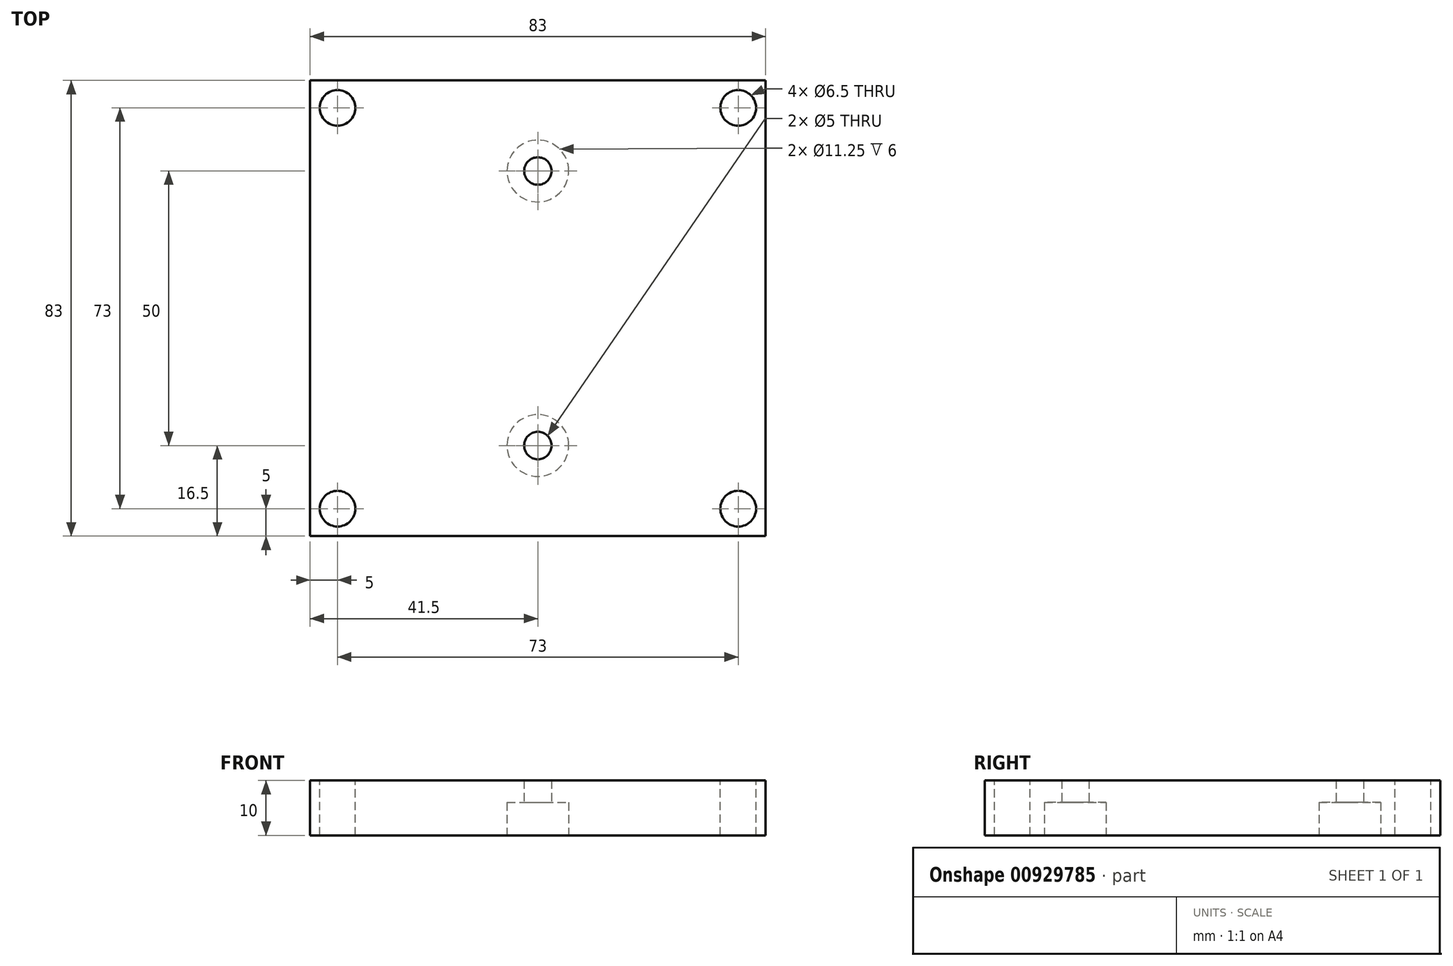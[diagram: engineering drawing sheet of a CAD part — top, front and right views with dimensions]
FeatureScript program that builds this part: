
annotation { "Feature Type Name" : "Feature", "Feature Type Description" : "" }
export const myFeature = defineFeature(function(context is Context, id is Id, definition is map)
    precondition{}
    {
        {
            var Q0;
            Q0=qCreatedBy(makeId("Top.planeOp"),FACE);
            var sketch = newSketch(context, id + "F0", { "sketchPlane" : qUnion([Q0])});
            skLineSegment(sketch, "E0.bottom", {"start": v(41.5, 41.5) * mm, "end": v(-41.5, 41.5) * mm});
            skLineSegment(sketch, "E0.top", {"start": v(41.5, -41.5) * mm, "end": v(-41.5, -41.5) * mm});
            skLineSegment(sketch, "E0.left", {"start": v(41.5, 41.5) * mm, "end": v(41.5, -41.5) * mm});
            skLineSegment(sketch, "E0.right", {"start": v(-41.5, 41.5) * mm, "end": v(-41.5, -41.5) * mm});
            skPoint(sketch, "E0.middle", {"position": v(0, 0) * mm});
            skSolve(sketch);
        }
        {
            var Q0;
            Q0 = qSketchRegion(id + "F0", true);
            extrude(context, id + "F1", {"entities" : qUnion([Q0]), "depth" : 10 * mm, "offsetDistance" : 25 * mm});
        }
        {
            var Q0;
            Q0=makeQuery(id+"F1.opExtrude","CAP_FACE",FACE,{"disambiguationData":[OSD([sQuery(id+"F0.wireOp",EDGE,"E0.bottom"),sQuery(id+"F0.wireOp",EDGE,"E0.top"),sQuery(id+"F0.wireOp",EDGE,"E0.left"),sQuery(id+"F0.wireOp",EDGE,"E0.right")])],"isStart":false});
            var sketch = newSketch(context, id + "F2", { "sketchPlane" : qUnion([Q0])});
            skLineSegment(sketch, "E1", {"start": v(71.1, 36.5) * mm, "end": v(-79.54, 36.5) * mm, "construction": true});
            skLineSegment(sketch, "E2", {"start": v(-78.9, -36.5) * mm, "end": v(83.67, -36.5) * mm, "construction": true});
            skLineSegment(sketch, "E3", {"start": v(-36.5, 85.44) * mm, "end": v(-36.5, -99.54) * mm, "construction": true});
            skLineSegment(sketch, "E4", {"start": v(36.5, 83.72) * mm, "end": v(36.5, -82.62) * mm, "construction": true});
            skCircle(sketch, "E5", {"center": v(-36.5, 36.5) * mm, "radius": 3.25 * mm});
            skCircle(sketch, "E6", {"center": v(-36.5, -36.5) * mm, "radius": 3.25 * mm});
            skCircle(sketch, "E7", {"center": v(36.5, -36.5) * mm, "radius": 3.25 * mm});
            skCircle(sketch, "E8", {"center": v(36.5, 36.5) * mm, "radius": 3.25 * mm});
            skSolve(sketch);
        }
        {
            var Q0;
            Q0 = qSketchRegion(id + "F2", true);
            extrude(context, id + "F3", {"entities" : qUnion([Q0]), "operationType" : NewBodyOperationType.REMOVE, "endBound" : BoundingType.UP_TO_NEXT, "oppositeDirection" : true, "depth" : 25 * mm, "offsetDistance" : 25 * mm});
        }
        {
            var Q0;
            Q0=makeQuery(id+"F1.opExtrude","CAP_FACE",FACE,{"disambiguationData":[OSD([sQuery(id+"F0.wireOp",EDGE,"E0.bottom"),sQuery(id+"F0.wireOp",EDGE,"E0.top"),sQuery(id+"F0.wireOp",EDGE,"E0.left"),sQuery(id+"F0.wireOp",EDGE,"E0.right")])],"isStart":true});
            var sketch = newSketch(context, id + "F4", { "sketchPlane" : qUnion([Q0])});
            skLineSegment(sketch, "E9", {"start": v(0, 41.5) * mm, "end": v(0, -41.5) * mm, "construction": true});
            skLineSegment(sketch, "E10", {"start": v(-41.5, 0) * mm, "end": v(41.5, 0) * mm, "construction": true});
            skLineSegment(sketch, "E11.0", {"start": v(-50, -25) * mm, "end": v(50, -25) * mm, "construction": true});
            skLineSegment(sketch, "E12.0", {"start": v(-50, 25) * mm, "end": v(50, 25) * mm, "construction": true});
            skLineSegment(sketch, "E13.0", {"start": v(46.5, 46.5) * mm, "end": v(-46.5, 46.5) * mm});
            skLineSegment(sketch, "E13.1", {"start": v(46.5, -46.5) * mm, "end": v(46.5, 46.5) * mm});
            skLineSegment(sketch, "E13.2", {"start": v(-46.5, -46.5) * mm, "end": v(46.5, -46.5) * mm});
            skLineSegment(sketch, "E13.3", {"start": v(-46.5, 46.5) * mm, "end": v(-46.5, -46.5) * mm});
            skCircle(sketch, "E14", {"center": v(0, -25) * mm, "radius": 2.5 * mm});
            skCircle(sketch, "E15", {"center": v(0, 25) * mm, "radius": 2.5 * mm});
            skSolve(sketch);
        }
        {
            var Q0;
            Q0=sQuery(id+"F4.wireOp",VERTEX,"E14.center");
            var Q1;
            Q1=sQuery(id+"F4.wireOp",VERTEX,"E15.center");
            var Q2;
            Q2=makeQuery(id+"F1.opExtrude","SWEPT_BODY",BODY,{"disambiguationData":[OSD([sQuery(id+"F0.wireOp",EDGE,"E0.bottom"),sQuery(id+"F0.wireOp",EDGE,"E0.top"),sQuery(id+"F0.wireOp",EDGE,"E0.left"),sQuery(id+"F0.wireOp",EDGE,"E0.right")])]});
            hole(context, id + "F5", {"style" : HoleStyle.C_BORE, "endStyle" : HoleEndStyle.BLIND, "standardTappedOrClearance" : lookupTablePath({ "standard" : "ISO", "engagement" : "75%", "pitch" : "1 mm", "size" : "M6", "type" : "Tapped" }), "standardBlindInLast" : lookupTablePath({ "standard" : "ISO", "engagement" : "75%", "pitch" : "1 mm", "size" : "M6", "type" : "Tapped" }), "holeDiameter" : 5 * mm, "cBoreDiameter" : 11.25 * mm, "cBoreDepth" : 6 * mm, "majorDiameter" : 6 * mm, "showTappedDepth" : true, "holeDepth" : 15 * mm, "isTappedThrough" : true, "tappedDepth" : 12 * mm, "tapClearance" : 3, "startFromSketch" : true, "locations" : qUnion([Q0, Q1]), "scope" : qUnion([Q2])});
        }
    });
